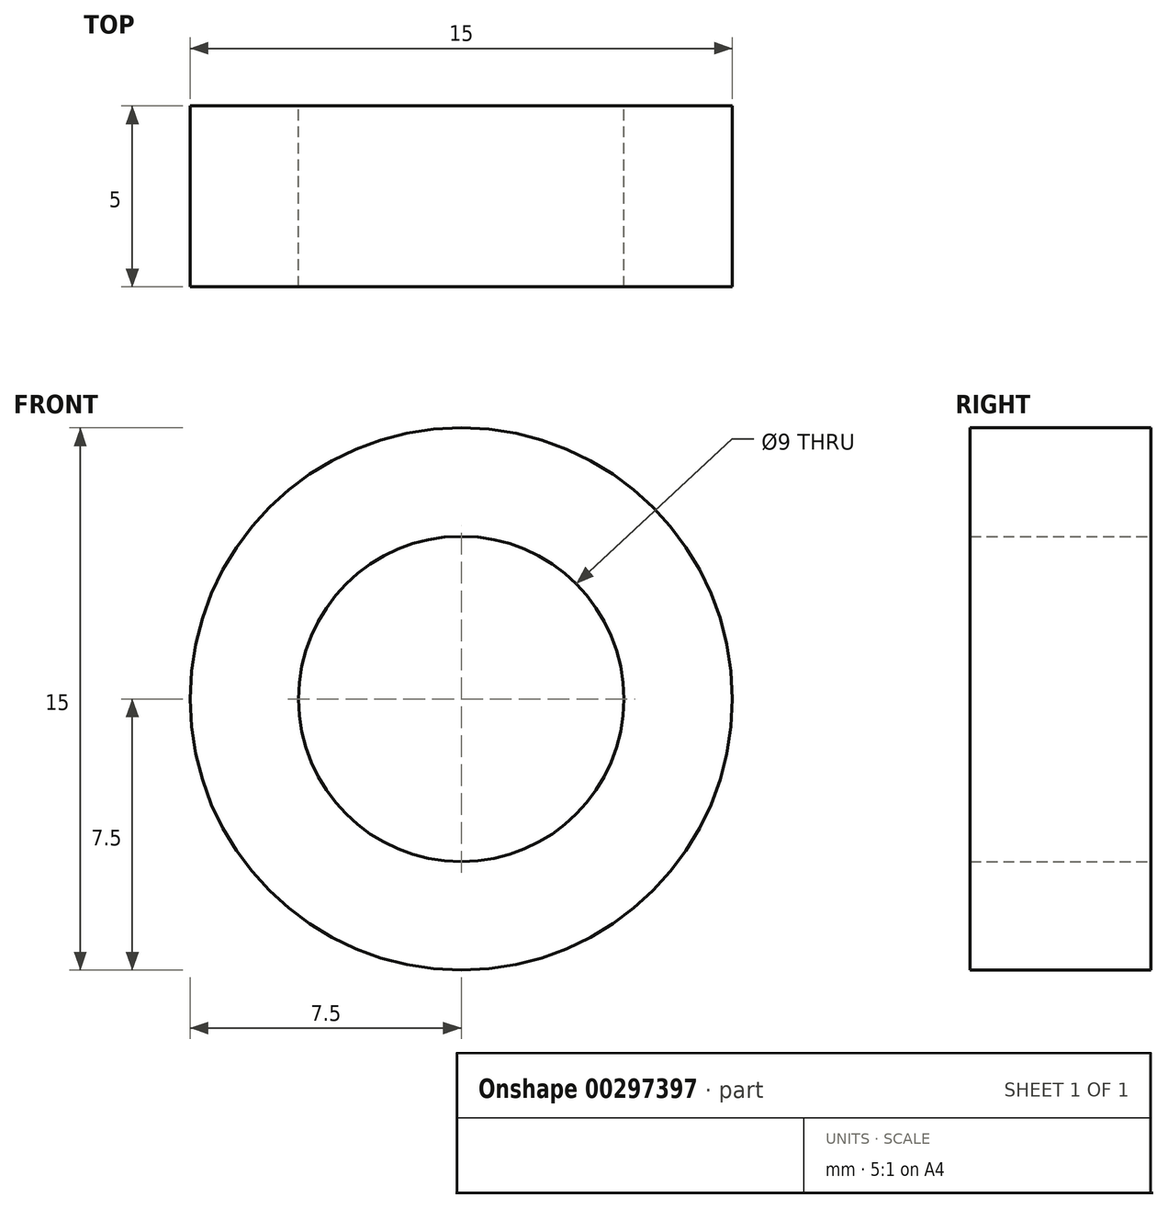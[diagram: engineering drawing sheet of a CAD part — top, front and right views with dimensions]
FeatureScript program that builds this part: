
annotation { "Feature Type Name" : "Feature", "Feature Type Description" : "" }
export const myFeature = defineFeature(function(context is Context, id is Id, definition is map)
    precondition{}
    {
        {
            var Q0;
            Q0=qCreatedBy(makeId("Front.planeOp"),FACE);
            var sketch = newSketch(context, id + "F0", { "sketchPlane" : qUnion([Q0])});
            skCircle(sketch, "E0", {"center": v(0, 0) * mm, "radius": 4.5 * mm});
            skCircle(sketch, "E1.0", {"center": v(0, 0) * mm, "radius": 7.5 * mm});
            skSolve(sketch);
        }
        {
            var Q0;
            Q0=makeQuery(id+"F0.imprint","IMPRINT",FACE,{"disambiguationData":[TD([[makeQuery(id+"F0.imprint","IMPRINT",EDGE,{"derivedFrom":sQuery(id+"F0.wireOp",EDGE,"E0")}),-1.0]])]});
            extrude(context, id + "F1", {"entities" : qUnion([Q0]), "depth" : 5 * mm});
        }
    });
